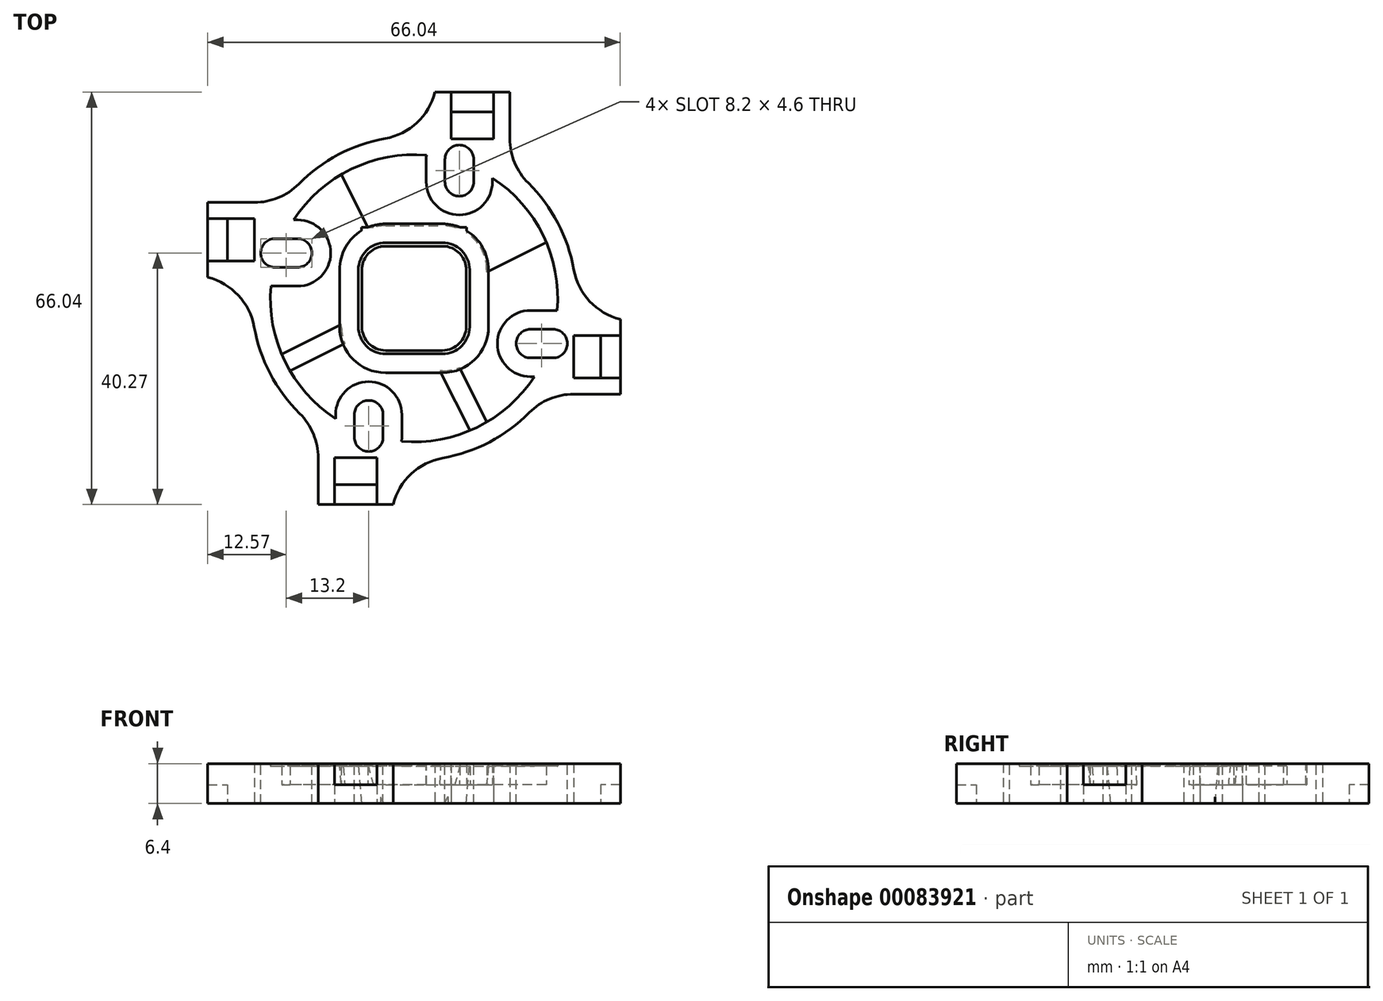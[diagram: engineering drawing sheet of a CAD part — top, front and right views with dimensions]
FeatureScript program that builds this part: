
annotation { "Feature Type Name" : "Feature", "Feature Type Description" : "" }
export const myFeature = defineFeature(function(context is Context, id is Id, definition is map)
    precondition{}
    {
        {
            var Q0;
            Q0=qCreatedBy(makeId("Top.planeOp"),FACE);
            var sketch = newSketch(context, id + "F0", { "sketchPlane" : qUnion([Q0])});
            skCircle(sketch, "E0", {"center": v(0, 0) * mm, "radius": 26 * mm});
            skLineSegment(sketch, "E1.bottom", {"start": v(4.55, 8.35) * mm, "end": v(-4.55, 8.35) * mm});
            skLineSegment(sketch, "E1.top", {"start": v(4.55, -8.35) * mm, "end": v(-4.55, -8.35) * mm});
            skLineSegment(sketch, "E1.left", {"start": v(8.35, 4.55) * mm, "end": v(8.35, -4.55) * mm});
            skLineSegment(sketch, "E1.right", {"start": v(-8.35, 4.55) * mm, "end": v(-8.35, -4.55) * mm});
            skPoint(sketch, "E2.visualSharp", {"position": v(8.35, 8.35) * mm});
            skArc(sketch, "E2.filletArc", {"start": v(8.35, 4.55) * mm, "mid": v(7.24, 7.24) * mm, "end": v(4.55, 8.35) * mm});
            skPoint(sketch, "E3.visualSharp", {"position": v(-8.35, 8.35) * mm});
            skArc(sketch, "E3.filletArc", {"start": v(-4.55, 8.35) * mm, "mid": v(-7.24, 7.24) * mm, "end": v(-8.35, 4.55) * mm});
            skPoint(sketch, "E4.visualSharp", {"position": v(-8.35, -8.35) * mm});
            skArc(sketch, "E4.filletArc", {"start": v(-8.35, -4.55) * mm, "mid": v(-7.24, -7.24) * mm, "end": v(-4.55, -8.35) * mm});
            skPoint(sketch, "E5.visualSharp", {"position": v(8.35, -8.35) * mm});
            skArc(sketch, "E5.filletArc", {"start": v(4.55, -8.35) * mm, "mid": v(7.24, -7.24) * mm, "end": v(8.35, -4.55) * mm});
            skLineSegment(sketch, "E6.bottom", {"start": v(-5.38, 8.35) * mm, "end": v(5.42, 8.35) * mm});
            skLineSegment(sketch, "E6.top", {"start": v(-5.38, 0) * mm, "end": v(5.42, 0) * mm});
            skLineSegment(sketch, "E6.left", {"start": v(-5.38, 8.35) * mm, "end": v(-5.38, 0) * mm});
            skLineSegment(sketch, "E6.right", {"start": v(5.42, 8.35) * mm, "end": v(5.42, 0) * mm});
            skArc(sketch, "E7", {"start": v(-5.38, 0) * mm, "mid": v(0.02, -5.4) * mm, "end": v(5.42, 0) * mm});
            skSolve(sketch);
        }
        {
            var Q0;
            Q0=makeQuery(id+"F0.imprint","IMPRINT",FACE,{"disambiguationData":[TD([[makeQuery(id+"F0.imprint","IMPRINT",EDGE,{"derivedFrom":sQuery(id+"F0.wireOp",EDGE,"E0")}),1.0]])]});
            var Q1;
            Q1=makeQuery(id+"F0.imprint","IMPRINT",FACE,{"disambiguationData":[TD([[makeQuery(id+"F0.imprint","IMPRINT",EDGE,{"derivedFrom":sQuery(id+"F0.wireOp",EDGE,"E1.top")}),-1.0]])]});
            var Q2;
            {var subQ0=sQuery(id+"F0.wireOp",EDGE,"E6.top");Q2=makeQuery(id+"F0.imprint","IMPRINT",FACE,{"disambiguationData":[TD([[makeQuery(id+"F0.imprint","IMPRINT",EDGE,{"derivedFrom":subQ0}),1.0]])]});}
            var Q3;
            Q3=makeQuery(id+"F0.imprint","IMPRINT",FACE,{"disambiguationData":[TD([[makeQuery(id+"F0.imprint","IMPRINT",EDGE,{"derivedFrom":sQuery(id+"F0.wireOp",EDGE,"E6.top")}),-1.0]])]});
            extrude(context, id + "F1", {"entities" : qUnion([Q0, Q1, Q2, Q3]), "depth" : 6.4 * mm});
        }
        {
            var Q0;
            {var subQ0=sQuery(id+"F0.wireOp",EDGE,"E6.top");Q0=makeQuery(id+"F0.imprint","IMPRINT",FACE,{"disambiguationData":[TD([[makeQuery(id+"F0.imprint","IMPRINT",EDGE,{"derivedFrom":subQ0}),1.0]])]});}
            var Q1;
            Q1=makeQuery(id+"F0.imprint","IMPRINT",FACE,{"disambiguationData":[TD([[makeQuery(id+"F0.imprint","IMPRINT",EDGE,{"derivedFrom":sQuery(id+"F0.wireOp",EDGE,"E6.top")}),-1.0]])]});
            var Q2;
            Q2=makeQuery(id+"F0.imprint","IMPRINT",FACE,{"disambiguationData":[TD([[makeQuery(id+"F0.imprint","IMPRINT",EDGE,{"derivedFrom":sQuery(id+"F0.wireOp",EDGE,"E1.top")}),-1.0]])]});
            extrude(context, id + "F2", {"entities" : qUnion([Q0, Q1, Q2]), "operationType" : NewBodyOperationType.REMOVE, "endBound" : BoundingType.THROUGH_ALL, "depth" : 25 * mm, "hasDraft" : true, "draftAngle" : 5 * degree});
        }
        {
            var Q0;
            Q0=qCreatedBy(makeId("Top.planeOp"),FACE);
            var sketch = newSketch(context, id + "F3", { "sketchPlane" : qUnion([Q0])});
            skLineSegment(sketch, "E8.bottom", {"start": v(3.35, 33.02) * mm, "end": v(15.35, 33.02) * mm});
            skLineSegment(sketch, "E8.top", {"start": v(3.35, 15.02) * mm, "end": v(15.35, 15.02) * mm});
            skLineSegment(sketch, "E8.left", {"start": v(3.35, 33.02) * mm, "end": v(3.35, 15.02) * mm});
            skLineSegment(sketch, "E8.right", {"start": v(15.35, 33.02) * mm, "end": v(15.35, 15.02) * mm});
            skLineSegment(sketch, "E9.bottom", {"start": v(5.95, 29.85) * mm, "end": v(12.75, 29.85) * mm});
            skLineSegment(sketch, "E9.top", {"start": v(5.95, 25.55) * mm, "end": v(12.75, 25.55) * mm});
            skLineSegment(sketch, "E9.left", {"start": v(5.95, 29.85) * mm, "end": v(5.95, 25.55) * mm});
            skLineSegment(sketch, "E9.right", {"start": v(12.75, 29.85) * mm, "end": v(12.75, 25.55) * mm});
            skLineSegment(sketch, "E10", {"start": v(12.75, 27.7) * mm, "end": v(15.35, 27.7) * mm, "construction": true});
            skLineSegment(sketch, "E11", {"start": v(5.95, 27.7) * mm, "end": v(3.35, 27.7) * mm, "construction": true});
            skSolve(sketch);
        }
        {
            var Q0;
            Q0 = qSketchRegion(id + "F3", true);
            extrude(context, id + "F4", {"entities" : qUnion([Q0]), "depth" : 6.4 * mm});
        }
        {
            var Q0;
            Q0=makeQuery(id+"F4.opExtrude","SWEPT_BODY",BODY,{"disambiguationData":[OSD([sQuery(id+"F3.wireOp",EDGE,"E8.bottom"),sQuery(id+"F3.wireOp",EDGE,"E8.top"),sQuery(id+"F3.wireOp",EDGE,"E8.left"),sQuery(id+"F3.wireOp",EDGE,"E8.right"),sQuery(id+"F3.wireOp",EDGE,"E9.bottom"),sQuery(id+"F3.wireOp",EDGE,"E9.top"),sQuery(id+"F3.wireOp",EDGE,"E9.left"),sQuery(id+"F3.wireOp",EDGE,"E9.right")])]});
            var Q1;
            Q1=makeQuery(id+"F1.opExtrude","SWEPT_FACE",FACE,{"disambiguationData":[OSD([sQuery(id+"F0.wireOp",EDGE,"E0")])]});
            circularPattern(context, id + "F5", {"entities" : qUnion([Q0]), "axis" : qUnion([Q1]), "angle" : 360 * degree, "instanceCount" : 4, "equalSpace" : true});
        }
        {
            var Q0;
            Q0=makeQuery(id+"F1.opExtrude","SWEPT_BODY",BODY,{"disambiguationData":[OSD([sQuery(id+"F0.wireOp",EDGE,"E0")])]});
            var Q1;
            Q1=makeQuery(id+"F5.opPattern","COPY",BODY,{"derivedFrom":makeQuery(id+"F4.opExtrude","SWEPT_BODY",BODY,{"disambiguationData":[OSD([sQuery(id+"F3.wireOp",EDGE,"E8.bottom"),sQuery(id+"F3.wireOp",EDGE,"E8.top"),sQuery(id+"F3.wireOp",EDGE,"E8.left"),sQuery(id+"F3.wireOp",EDGE,"E8.right"),sQuery(id+"F3.wireOp",EDGE,"E9.bottom"),sQuery(id+"F3.wireOp",EDGE,"E9.top"),sQuery(id+"F3.wireOp",EDGE,"E9.left"),sQuery(id+"F3.wireOp",EDGE,"E9.right")])]}),"instanceName":"3"});
            var Q2;
            Q2=makeQuery(id+"F4.opExtrude","SWEPT_BODY",BODY,{"disambiguationData":[OSD([sQuery(id+"F3.wireOp",EDGE,"E8.bottom"),sQuery(id+"F3.wireOp",EDGE,"E8.top"),sQuery(id+"F3.wireOp",EDGE,"E8.left"),sQuery(id+"F3.wireOp",EDGE,"E8.right"),sQuery(id+"F3.wireOp",EDGE,"E9.bottom"),sQuery(id+"F3.wireOp",EDGE,"E9.top"),sQuery(id+"F3.wireOp",EDGE,"E9.left"),sQuery(id+"F3.wireOp",EDGE,"E9.right")])]});
            var Q3;
            Q3=makeQuery(id+"F5.opPattern","COPY",BODY,{"derivedFrom":makeQuery(id+"F4.opExtrude","SWEPT_BODY",BODY,{"disambiguationData":[OSD([sQuery(id+"F3.wireOp",EDGE,"E8.bottom"),sQuery(id+"F3.wireOp",EDGE,"E8.top"),sQuery(id+"F3.wireOp",EDGE,"E8.left"),sQuery(id+"F3.wireOp",EDGE,"E8.right"),sQuery(id+"F3.wireOp",EDGE,"E9.bottom"),sQuery(id+"F3.wireOp",EDGE,"E9.top"),sQuery(id+"F3.wireOp",EDGE,"E9.left"),sQuery(id+"F3.wireOp",EDGE,"E9.right")])]}),"instanceName":"2"});
            var Q4;
            Q4=makeQuery(id+"F5.opPattern","COPY",BODY,{"derivedFrom":makeQuery(id+"F4.opExtrude","SWEPT_BODY",BODY,{"disambiguationData":[OSD([sQuery(id+"F3.wireOp",EDGE,"E8.bottom"),sQuery(id+"F3.wireOp",EDGE,"E8.top"),sQuery(id+"F3.wireOp",EDGE,"E8.left"),sQuery(id+"F3.wireOp",EDGE,"E8.right"),sQuery(id+"F3.wireOp",EDGE,"E9.bottom"),sQuery(id+"F3.wireOp",EDGE,"E9.top"),sQuery(id+"F3.wireOp",EDGE,"E9.left"),sQuery(id+"F3.wireOp",EDGE,"E9.right")])]}),"instanceName":"1"});
            booleanBodies(context, id + "F6", {"operationType" : BooleanOperationType.UNION, "tools" : qUnion([Q0, Q1, Q2, Q3, Q4])});
        }
        {
            var Q0;
            {var subQ0=makeQuery(id+"F4.opExtrude","CAP_FACE",FACE,{"disambiguationData":[OSD([sQuery(id+"F3.wireOp",EDGE,"E8.bottom"),sQuery(id+"F3.wireOp",EDGE,"E8.top"),sQuery(id+"F3.wireOp",EDGE,"E8.left"),sQuery(id+"F3.wireOp",EDGE,"E8.right"),sQuery(id+"F3.wireOp",EDGE,"E9.bottom"),sQuery(id+"F3.wireOp",EDGE,"E9.top"),sQuery(id+"F3.wireOp",EDGE,"E9.left"),sQuery(id+"F3.wireOp",EDGE,"E9.right")])],"isStart":false});Q0=makeQuery(id+"F6.opBoolean","MERGE",FACE,{"derivedFrom":[makeQuery(id+"F1.opExtrude","CAP_FACE",FACE,{"disambiguationData":[OSD([sQuery(id+"F0.wireOp",EDGE,"E0")])],"isStart":false}),subQ0,makeQuery(id+"F5.opPattern","COPY",FACE,{"derivedFrom":subQ0,"instanceName":"1"}),makeQuery(id+"F5.opPattern","COPY",FACE,{"derivedFrom":subQ0,"instanceName":"2"}),makeQuery(id+"F5.opPattern","COPY",FACE,{"derivedFrom":subQ0,"instanceName":"3"})]});}
            var sketch = newSketch(context, id + "F7", { "sketchPlane" : qUnion([Q0])});
            skLineSegment(sketch, "E12.bottom", {"start": v(4.95, 22.25) * mm, "end": v(9.55, 22.25) * mm});
            skLineSegment(sketch, "E12.top", {"start": v(4.95, 18.65) * mm, "end": v(9.55, 18.65) * mm});
            skLineSegment(sketch, "E12.left", {"start": v(4.95, 22.25) * mm, "end": v(4.95, 18.65) * mm});
            skLineSegment(sketch, "E12.right", {"start": v(9.55, 22.25) * mm, "end": v(9.55, 18.65) * mm});
            skArc(sketch, "E13", {"start": v(9.55, 22.25) * mm, "mid": v(7.25, 24.55) * mm, "end": v(4.95, 22.25) * mm});
            skArc(sketch, "E14", {"start": v(4.95, 18.65) * mm, "mid": v(7.25, 16.35) * mm, "end": v(9.55, 18.65) * mm});
            skArc(sketch, "E15.1.0", {"start": v(-18.65, 4.95) * mm, "mid": v(-16.35, 7.25) * mm, "end": v(-18.65, 9.55) * mm});
            skLineSegment(sketch, "E15.1.1", {"start": v(-22.25, 9.55) * mm, "end": v(-18.65, 9.55) * mm});
            skArc(sketch, "E15.1.2", {"start": v(-22.25, 9.55) * mm, "mid": v(-24.55, 7.25) * mm, "end": v(-22.25, 4.95) * mm});
            skLineSegment(sketch, "E15.1.3", {"start": v(-18.65, 4.95) * mm, "end": v(-18.65, 9.55) * mm});
            skLineSegment(sketch, "E15.1.4", {"start": v(-22.25, 4.95) * mm, "end": v(-22.25, 9.55) * mm});
            skLineSegment(sketch, "E15.1.5", {"start": v(-22.25, 4.95) * mm, "end": v(-18.65, 4.95) * mm});
            skArc(sketch, "E15.2.0", {"start": v(-4.95, -18.65) * mm, "mid": v(-7.25, -16.35) * mm, "end": v(-9.55, -18.65) * mm});
            skLineSegment(sketch, "E15.2.1", {"start": v(-9.55, -22.25) * mm, "end": v(-9.55, -18.65) * mm});
            skArc(sketch, "E15.2.2", {"start": v(-9.55, -22.25) * mm, "mid": v(-7.25, -24.55) * mm, "end": v(-4.95, -22.25) * mm});
            skLineSegment(sketch, "E15.2.3", {"start": v(-4.95, -18.65) * mm, "end": v(-9.55, -18.65) * mm});
            skLineSegment(sketch, "E15.2.4", {"start": v(-4.95, -22.25) * mm, "end": v(-9.55, -22.25) * mm});
            skLineSegment(sketch, "E15.2.5", {"start": v(-4.95, -22.25) * mm, "end": v(-4.95, -18.65) * mm});
            skArc(sketch, "E15.3.0", {"start": v(18.65, -4.95) * mm, "mid": v(16.35, -7.25) * mm, "end": v(18.65, -9.55) * mm});
            skLineSegment(sketch, "E15.3.1", {"start": v(22.25, -9.55) * mm, "end": v(18.65, -9.55) * mm});
            skArc(sketch, "E15.3.2", {"start": v(22.25, -9.55) * mm, "mid": v(24.55, -7.25) * mm, "end": v(22.25, -4.95) * mm});
            skLineSegment(sketch, "E15.3.3", {"start": v(18.65, -4.95) * mm, "end": v(18.65, -9.55) * mm});
            skLineSegment(sketch, "E15.3.4", {"start": v(22.25, -4.95) * mm, "end": v(22.25, -9.55) * mm});
            skLineSegment(sketch, "E15.3.5", {"start": v(22.25, -4.95) * mm, "end": v(18.65, -4.95) * mm});
            skPoint(sketch, "E15.center", {"position": v(0, 0) * mm});
            skSolve(sketch);
        }
        {
            var Q0;
            Q0 = qSketchRegion(id + "F7", true);
            extrude(context, id + "F8", {"entities" : qUnion([Q0]), "operationType" : NewBodyOperationType.REMOVE, "endBound" : BoundingType.THROUGH_ALL, "oppositeDirection" : true, "depth" : 25 * mm});
        }
        {
            var Q0;
            {var subQ0=makeQuery(id+"F4.opExtrude","CAP_FACE",FACE,{"disambiguationData":[OSD([sQuery(id+"F3.wireOp",EDGE,"E8.bottom"),sQuery(id+"F3.wireOp",EDGE,"E8.top"),sQuery(id+"F3.wireOp",EDGE,"E8.left"),sQuery(id+"F3.wireOp",EDGE,"E8.right"),sQuery(id+"F3.wireOp",EDGE,"E9.bottom"),sQuery(id+"F3.wireOp",EDGE,"E9.top"),sQuery(id+"F3.wireOp",EDGE,"E9.left"),sQuery(id+"F3.wireOp",EDGE,"E9.right")])],"isStart":false});Q0=makeQuery(id+"F6.opBoolean","MERGE",FACE,{"derivedFrom":[makeQuery(id+"F1.opExtrude","CAP_FACE",FACE,{"disambiguationData":[OSD([sQuery(id+"F0.wireOp",EDGE,"E0")])],"isStart":false}),subQ0,makeQuery(id+"F5.opPattern","COPY",FACE,{"derivedFrom":subQ0,"instanceName":"1"}),makeQuery(id+"F5.opPattern","COPY",FACE,{"derivedFrom":subQ0,"instanceName":"2"}),makeQuery(id+"F5.opPattern","COPY",FACE,{"derivedFrom":subQ0,"instanceName":"3"})]});}
            var sketch = newSketch(context, id + "F9", { "sketchPlane" : qUnion([Q0])});
            skLineSegment(sketch, "E16.bottom", {"start": v(5.95, 33.02) * mm, "end": v(12.75, 33.02) * mm});
            skLineSegment(sketch, "E16.top", {"start": v(5.95, 25.55) * mm, "end": v(12.75, 25.55) * mm});
            skLineSegment(sketch, "E16.left", {"start": v(5.95, 33.02) * mm, "end": v(5.95, 25.55) * mm});
            skLineSegment(sketch, "E16.right", {"start": v(12.75, 33.02) * mm, "end": v(12.75, 25.55) * mm});
            skLineSegment(sketch, "E17.1.0", {"start": v(-33.02, 12.75) * mm, "end": v(-25.55, 12.75) * mm});
            skLineSegment(sketch, "E17.1.1", {"start": v(-33.02, 5.95) * mm, "end": v(-25.55, 5.95) * mm});
            skLineSegment(sketch, "E17.1.2", {"start": v(-25.55, 5.95) * mm, "end": v(-25.55, 12.75) * mm});
            skLineSegment(sketch, "E17.1.3", {"start": v(-33.02, 5.95) * mm, "end": v(-33.02, 12.75) * mm});
            skLineSegment(sketch, "E17.2.0", {"start": v(-12.75, -33.02) * mm, "end": v(-12.75, -25.55) * mm});
            skLineSegment(sketch, "E17.2.1", {"start": v(-5.95, -33.02) * mm, "end": v(-5.95, -25.55) * mm});
            skLineSegment(sketch, "E17.2.2", {"start": v(-5.95, -25.55) * mm, "end": v(-12.75, -25.55) * mm});
            skLineSegment(sketch, "E17.2.3", {"start": v(-5.95, -33.02) * mm, "end": v(-12.75, -33.02) * mm});
            skLineSegment(sketch, "E17.3.0", {"start": v(33.02, -12.75) * mm, "end": v(25.55, -12.75) * mm});
            skLineSegment(sketch, "E17.3.1", {"start": v(33.02, -5.95) * mm, "end": v(25.55, -5.95) * mm});
            skLineSegment(sketch, "E17.3.2", {"start": v(25.55, -5.95) * mm, "end": v(25.55, -12.75) * mm});
            skLineSegment(sketch, "E17.3.3", {"start": v(33.02, -5.95) * mm, "end": v(33.02, -12.75) * mm});
            skPoint(sketch, "E17.center", {"position": v(0, 0) * mm});
            skSolve(sketch);
        }
        {
            var Q0;
            Q0 = qSketchRegion(id + "F9", true);
            extrude(context, id + "F10", {"entities" : qUnion([Q0]), "operationType" : NewBodyOperationType.REMOVE, "oppositeDirection" : true, "depth" : 3.4 * mm});
        }
        {
            var Q0;
            {var subQ0=makeQuery(id+"F4.opExtrude","CAP_FACE",FACE,{"disambiguationData":[OSD([sQuery(id+"F3.wireOp",EDGE,"E8.bottom"),sQuery(id+"F3.wireOp",EDGE,"E8.top"),sQuery(id+"F3.wireOp",EDGE,"E8.left"),sQuery(id+"F3.wireOp",EDGE,"E8.right"),sQuery(id+"F3.wireOp",EDGE,"E9.bottom"),sQuery(id+"F3.wireOp",EDGE,"E9.top"),sQuery(id+"F3.wireOp",EDGE,"E9.left"),sQuery(id+"F3.wireOp",EDGE,"E9.right")])],"isStart":false});Q0=makeQuery(id+"F6.opBoolean","MERGE",FACE,{"derivedFrom":[makeQuery(id+"F1.opExtrude","CAP_FACE",FACE,{"disambiguationData":[OSD([sQuery(id+"F0.wireOp",EDGE,"E0")])],"isStart":false}),subQ0,makeQuery(id+"F5.opPattern","COPY",FACE,{"derivedFrom":subQ0,"instanceName":"1"}),makeQuery(id+"F5.opPattern","COPY",FACE,{"derivedFrom":subQ0,"instanceName":"2"}),makeQuery(id+"F5.opPattern","COPY",FACE,{"derivedFrom":subQ0,"instanceName":"3"})]});}
            shell(context, id + "F11", {"entities" : qUnion([Q0]), "thickness" : 3 * mm});
        }
        {
            var Q0;
            Q0=makeQuery(id+"F6.opBoolean","INTERSECT",EDGE,{"derivedFrom":[makeQuery(id+"F1.opExtrude","SWEPT_FACE",FACE,{"disambiguationData":[OSD([sQuery(id+"F0.wireOp",EDGE,"E0")])]}),makeQuery(id+"F4.opExtrude","SWEPT_FACE",FACE,{"disambiguationData":[OSD([sQuery(id+"F3.wireOp",EDGE,"E8.left")])]})]});
            var Q1;
            Q1=makeQuery(id+"F6.opBoolean","INTERSECT",EDGE,{"derivedFrom":[makeQuery(id+"F1.opExtrude","SWEPT_FACE",FACE,{"disambiguationData":[OSD([sQuery(id+"F0.wireOp",EDGE,"E0")])]}),makeQuery(id+"F5.opPattern","COPY",FACE,{"derivedFrom":makeQuery(id+"F4.opExtrude","SWEPT_FACE",FACE,{"disambiguationData":[OSD([sQuery(id+"F3.wireOp",EDGE,"E8.right")])]}),"instanceName":"3"})]});
            var Q2;
            Q2=makeQuery(id+"F6.opBoolean","INTERSECT",EDGE,{"derivedFrom":[makeQuery(id+"F1.opExtrude","SWEPT_FACE",FACE,{"disambiguationData":[OSD([sQuery(id+"F0.wireOp",EDGE,"E0")])]}),makeQuery(id+"F5.opPattern","COPY",FACE,{"derivedFrom":makeQuery(id+"F4.opExtrude","SWEPT_FACE",FACE,{"disambiguationData":[OSD([sQuery(id+"F3.wireOp",EDGE,"E8.left")])]}),"instanceName":"3"})]});
            var Q3;
            Q3=makeQuery(id+"F6.opBoolean","INTERSECT",EDGE,{"derivedFrom":[makeQuery(id+"F1.opExtrude","SWEPT_FACE",FACE,{"disambiguationData":[OSD([sQuery(id+"F0.wireOp",EDGE,"E0")])]}),makeQuery(id+"F5.opPattern","COPY",FACE,{"derivedFrom":makeQuery(id+"F4.opExtrude","SWEPT_FACE",FACE,{"disambiguationData":[OSD([sQuery(id+"F3.wireOp",EDGE,"E8.right")])]}),"instanceName":"2"})]});
            var Q4;
            Q4=makeQuery(id+"F6.opBoolean","INTERSECT",EDGE,{"derivedFrom":[makeQuery(id+"F1.opExtrude","SWEPT_FACE",FACE,{"disambiguationData":[OSD([sQuery(id+"F0.wireOp",EDGE,"E0")])]}),makeQuery(id+"F5.opPattern","COPY",FACE,{"derivedFrom":makeQuery(id+"F4.opExtrude","SWEPT_FACE",FACE,{"disambiguationData":[OSD([sQuery(id+"F3.wireOp",EDGE,"E8.left")])]}),"instanceName":"2"})]});
            var Q5;
            Q5=makeQuery(id+"F6.opBoolean","INTERSECT",EDGE,{"derivedFrom":[makeQuery(id+"F1.opExtrude","SWEPT_FACE",FACE,{"disambiguationData":[OSD([sQuery(id+"F0.wireOp",EDGE,"E0")])]}),makeQuery(id+"F5.opPattern","COPY",FACE,{"derivedFrom":makeQuery(id+"F4.opExtrude","SWEPT_FACE",FACE,{"disambiguationData":[OSD([sQuery(id+"F3.wireOp",EDGE,"E8.right")])]}),"instanceName":"1"})]});
            var Q6;
            Q6=makeQuery(id+"F6.opBoolean","INTERSECT",EDGE,{"derivedFrom":[makeQuery(id+"F1.opExtrude","SWEPT_FACE",FACE,{"disambiguationData":[OSD([sQuery(id+"F0.wireOp",EDGE,"E0")])]}),makeQuery(id+"F5.opPattern","COPY",FACE,{"derivedFrom":makeQuery(id+"F4.opExtrude","SWEPT_FACE",FACE,{"disambiguationData":[OSD([sQuery(id+"F3.wireOp",EDGE,"E8.left")])]}),"instanceName":"1"})]});
            var Q7;
            Q7=makeQuery(id+"F6.opBoolean","INTERSECT",EDGE,{"derivedFrom":[makeQuery(id+"F1.opExtrude","SWEPT_FACE",FACE,{"disambiguationData":[OSD([sQuery(id+"F0.wireOp",EDGE,"E0")])]}),makeQuery(id+"F4.opExtrude","SWEPT_FACE",FACE,{"disambiguationData":[OSD([sQuery(id+"F3.wireOp",EDGE,"E8.right")])]})]});
            fillet(context, id + "F12", {"entities" : qUnion([Q0, Q1, Q2, Q3, Q4, Q5, Q6, Q7]), "radius" : 10 * mm, "tangentPropagation" : true, "allowEdgeOverflow" : false});
        }
        {
            var Q0;
            {var subQ0=sQuery(id+"F3.wireOp",EDGE,"E9.right");var subQ1=sQuery(id+"F3.wireOp",EDGE,"E9.left");var subQ2=sQuery(id+"F3.wireOp",EDGE,"E9.top");var subQ3=sQuery(id+"F3.wireOp",EDGE,"E9.bottom");var subQ4=sQuery(id+"F3.wireOp",EDGE,"E8.right");var subQ5=sQuery(id+"F3.wireOp",EDGE,"E8.left");var subQ6=sQuery(id+"F3.wireOp",EDGE,"E8.top");var subQ7=sQuery(id+"F3.wireOp",EDGE,"E8.bottom");var subQ8=makeQuery(id+"F4.opExtrude","CAP_FACE",FACE,{"disambiguationData":[OSD([subQ7,subQ6,subQ5,subQ4,subQ3,subQ2,subQ1,subQ0])],"isStart":true});var subQ9=sQuery(id+"F0.wireOp",EDGE,"E0");Q0=makeQuery(id+"F11.opShell","OFFSET_FACE",FACE,{"disambiguationData":[OSD([subQ9,subQ7,subQ6,subQ5,subQ4,subQ3,subQ2,subQ1,subQ0]),TDD([makeQuery(id+"F6.opBoolean","MERGE",FACE,{"derivedFrom":[makeQuery(id+"F1.opExtrude","CAP_FACE",FACE,{"disambiguationData":[OSD([subQ9])],"isStart":true}),subQ8,makeQuery(id+"F5.opPattern","COPY",FACE,{"derivedFrom":subQ8,"instanceName":"1"}),makeQuery(id+"F5.opPattern","COPY",FACE,{"derivedFrom":subQ8,"instanceName":"2"}),makeQuery(id+"F5.opPattern","COPY",FACE,{"derivedFrom":subQ8,"instanceName":"3"})]})])]});}
            var sketch = newSketch(context, id + "F13", { "sketchPlane" : qUnion([Q0])});
            skLineSegment(sketch, "E18", {"start": v(-11.65, 19.83) * mm, "end": v(8.97, -21.18) * mm});
            skLineSegment(sketch, "E19", {"start": v(-8.97, 21.18) * mm, "end": v(11.65, -19.83) * mm});
            skLineSegment(sketch, "E20", {"start": v(-1.34, -0.67) * mm, "end": v(1.34, 0.67) * mm, "construction": true});
            skLineSegment(sketch, "E21.1.0", {"start": v(21.18, 8.97) * mm, "end": v(-19.83, -11.65) * mm});
            skLineSegment(sketch, "E21.1.1", {"start": v(19.83, 11.65) * mm, "end": v(-21.18, -8.97) * mm});
            skLineSegment(sketch, "E21.1.2", {"start": v(-0.67, 1.34) * mm, "end": v(0.67, -1.34) * mm, "construction": true});
            skPoint(sketch, "E21.center", {"position": v(0, 0) * mm});
            skLineSegment(sketch, "E21.anchor1", {"start": v(0, 0) * mm, "end": v(11.65, -19.83) * mm, "construction": true});
            skLineSegment(sketch, "E21.anchor2", {"start": v(0, 0) * mm, "end": v(-19.83, -11.65) * mm, "construction": true});
            skCircle(sketch, "E22", {"center": v(0, 0) * mm, "radius": 23 * mm});
            skSolve(sketch);
        }
        {
            var Q0;
            {var subQ7=sQuery(id+"F13.wireOp",EDGE,"E22");var subQ8=sQuery(id+"F13.wireOp",EDGE,"E18");var subQ9=makeQuery(id+"F13.imprint","INTERSECT",VERTEX,{"disambiguationData":[OD(0.0)],"derivedFrom":[subQ8,subQ7]});Q0=makeQuery(id+"F13.imprint","IMPRINT",FACE,{"disambiguationData":[TD([[makeQuery(id+"F13.imprint","IMPRINT",EDGE,{"disambiguationData":[TD([[subQ9,1.0]])],"derivedFrom":subQ7}),1.0]])]});}
            var Q1;
            {var subQ0=sQuery(id+"F13.wireOp",EDGE,"E22");var subQ9=sQuery(id+"F13.wireOp",EDGE,"E21.1.0");var subQ10=makeQuery(id+"F13.imprint","INTERSECT",VERTEX,{"disambiguationData":[OD(1.0)],"derivedFrom":[subQ9,subQ0]});Q1=makeQuery(id+"F13.imprint","IMPRINT",FACE,{"disambiguationData":[TD([[makeQuery(id+"F13.imprint","IMPRINT",EDGE,{"disambiguationData":[TD([[subQ10,1.0]])],"derivedFrom":subQ0}),1.0]])]});}
            var Q2;
            {var subQ0=sQuery(id+"F13.wireOp",EDGE,"E22");var subQ1=sQuery(id+"F13.wireOp",EDGE,"E18");var subQ2=makeQuery(id+"F13.imprint","INTERSECT",VERTEX,{"disambiguationData":[OD(1.0)],"derivedFrom":[subQ1,subQ0]});Q2=makeQuery(id+"F13.imprint","IMPRINT",FACE,{"disambiguationData":[TD([[makeQuery(id+"F13.imprint","IMPRINT",EDGE,{"disambiguationData":[TD([[subQ2,-1.0]])],"derivedFrom":subQ0}),1.0]])]});}
            var Q3;
            {var subQ0=sQuery(id+"F13.wireOp",EDGE,"E22");var subQ1=sQuery(id+"F13.wireOp",EDGE,"E21.1.0");var subQ2=makeQuery(id+"F13.imprint","INTERSECT",VERTEX,{"disambiguationData":[OD(0.0)],"derivedFrom":[subQ1,subQ0]});Q3=makeQuery(id+"F13.imprint","IMPRINT",FACE,{"disambiguationData":[TD([[makeQuery(id+"F13.imprint","IMPRINT",EDGE,{"disambiguationData":[TD([[subQ2,-1.0]])],"derivedFrom":subQ0}),1.0]])]});}
            extrude(context, id + "F14", {"entities" : qUnion([Q0, Q1, Q2, Q3]), "operationType" : NewBodyOperationType.ADD, "depth" : 3 * mm});
        }
    });
